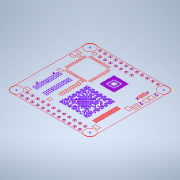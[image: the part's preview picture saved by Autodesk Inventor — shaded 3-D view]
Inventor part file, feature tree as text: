
AUTODESK INVENTOR PART (.ipt)
format: ipt  version: 2021 (Build 250183000, 183)  size: 396,288 bytes
history: native  units: mm
features: sketch x1
ambient origin geometry x8: Origin, YZ Plane, XZ Plane, XY Plane, X Axis, Y Axis, Z Axis, Center Point
feature tree (1):
  sketch  "Sketch1"
